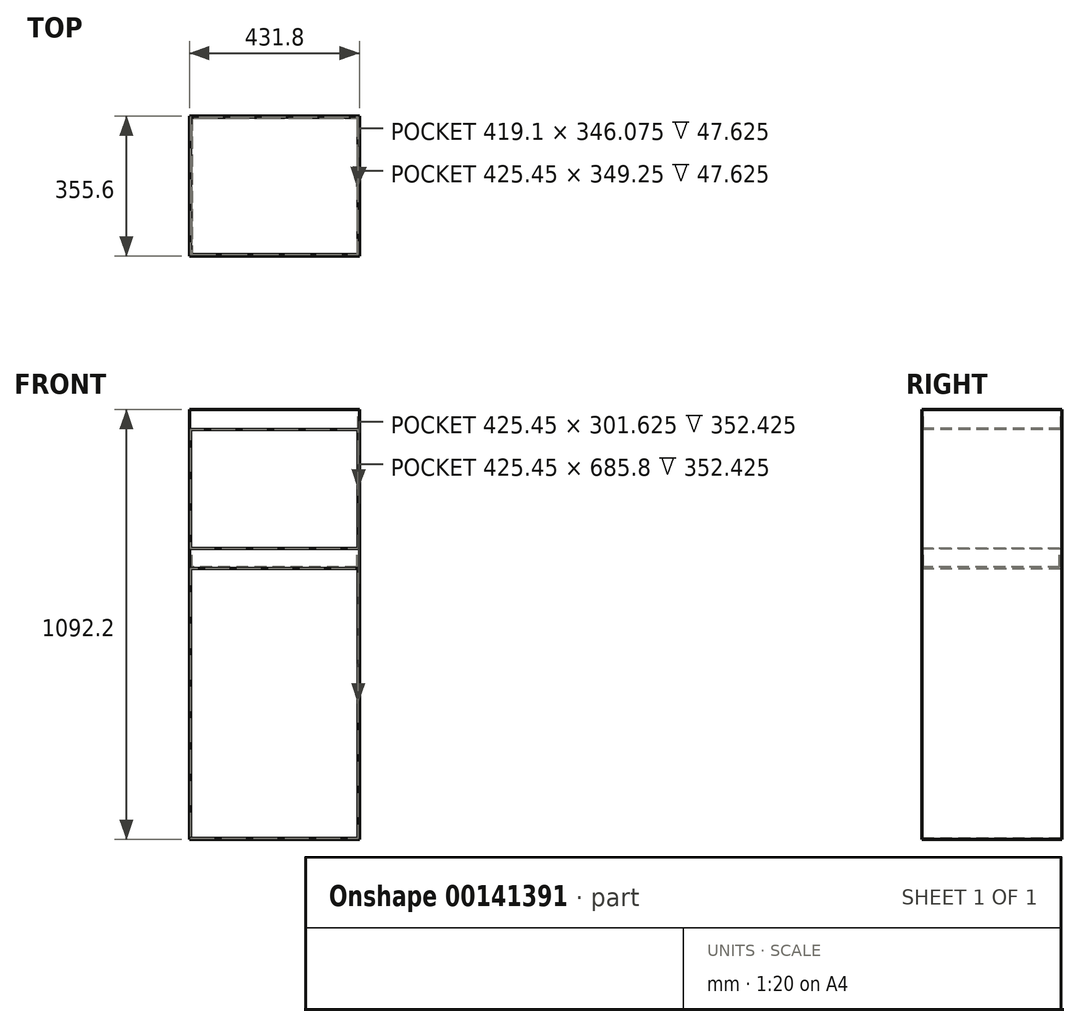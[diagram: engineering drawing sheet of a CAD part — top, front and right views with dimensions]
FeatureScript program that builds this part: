
annotation { "Feature Type Name" : "Feature", "Feature Type Description" : "" }
export const myFeature = defineFeature(function(context is Context, id is Id, definition is map)
    precondition{}
    {
        {
            var Q0;
            Q0=qCreatedBy(makeId("Front.planeOp"),FACE);
            var sketch = newSketch(context, id + "F0", { "sketchPlane" : qUnion([Q0])});
            skLineSegment(sketch, "E0.bottom", {"start": v(-215.9, 546.1) * mm, "end": v(215.9, 546.1) * mm});
            skLineSegment(sketch, "E0.top", {"start": v(-215.9, -546.1) * mm, "end": v(215.9, -546.1) * mm});
            skLineSegment(sketch, "E0.left", {"start": v(-215.9, 546.1) * mm, "end": v(-215.9, -546.1) * mm});
            skLineSegment(sketch, "E0.right", {"start": v(215.9, 546.1) * mm, "end": v(215.9, -546.1) * mm});
            skPoint(sketch, "E0.middle", {"position": v(0, 0) * mm});
            skSolve(sketch);
        }
        {
            var Q0;
            Q0 = qSketchRegion(id + "F0", true);
            extrude(context, id + "F1", {"entities" : qUnion([Q0]), "depth" : 355.6 * mm});
        }
        {
            var Q0;
            Q0=makeQuery(id+"F1.opExtrude","CAP_FACE",FACE,{"disambiguationData":[OSD([sQuery(id+"F0.wireOp",EDGE,"E0.bottom"),sQuery(id+"F0.wireOp",EDGE,"E0.top"),sQuery(id+"F0.wireOp",EDGE,"E0.left"),sQuery(id+"F0.wireOp",EDGE,"E0.right")])],"isStart":false});
            var sketch = newSketch(context, id + "F2", { "sketchPlane" : qUnion([Q0])});
            skLineSegment(sketch, "E1.bottom", {"start": v(-212.72, 495.3) * mm, "end": v(212.73, 495.3) * mm});
            skLineSegment(sketch, "E1.top", {"start": v(-212.72, -542.92) * mm, "end": v(212.73, -542.92) * mm});
            skLineSegment(sketch, "E1.left", {"start": v(-212.72, 495.3) * mm, "end": v(-212.73, -542.92) * mm});
            skLineSegment(sketch, "E1.right", {"start": v(212.72, 495.3) * mm, "end": v(212.73, -542.92) * mm});
            skSolve(sketch);
        }
        {
            var Q0;
            Q0 = qSketchRegion(id + "F2", true);
            extrude(context, id + "F3", {"entities" : qUnion([Q0]), "operationType" : NewBodyOperationType.REMOVE, "oppositeDirection" : true, "depth" : 352.42 * mm});
        }
        {
            var Q0;
            Q0=makeQuery(id+"F3.boolean.opBoolean","COPY",FACE,{"derivedFrom":makeQuery(id+"F3.opExtrude","CAP_FACE",FACE,{"disambiguationData":[OSD([sQuery(id+"F2.wireOp",EDGE,"E1.bottom"),sQuery(id+"F2.wireOp",EDGE,"E1.top"),sQuery(id+"F2.wireOp",EDGE,"E1.left"),sQuery(id+"F2.wireOp",EDGE,"E1.right")])],"isStart":false})});
            var sketch = newSketch(context, id + "F4", { "sketchPlane" : qUnion([Q0])});
            skLineSegment(sketch, "E2.bottom", {"start": v(-212.72, 193.68) * mm, "end": v(212.73, 193.68) * mm});
            skLineSegment(sketch, "E2.top", {"start": v(-212.72, 142.88) * mm, "end": v(212.73, 142.88) * mm});
            skLineSegment(sketch, "E2.left", {"start": v(-212.72, 193.68) * mm, "end": v(-212.72, 142.88) * mm});
            skLineSegment(sketch, "E2.right", {"start": v(212.73, 193.68) * mm, "end": v(212.73, 142.88) * mm});
            skSolve(sketch);
        }
        {
            var Q0;
            Q0 = qSketchRegion(id + "F4", true);
            var Q1;
            Q1=makeQuery(id+"F1.opExtrude","CAP_FACE",FACE,{"disambiguationData":[OSD([sQuery(id+"F0.wireOp",EDGE,"E0.bottom"),sQuery(id+"F0.wireOp",EDGE,"E0.top"),sQuery(id+"F0.wireOp",EDGE,"E0.left"),sQuery(id+"F0.wireOp",EDGE,"E0.right")])],"isStart":false});
            extrude(context, id + "F5", {"entities" : qUnion([Q0]), "operationType" : NewBodyOperationType.ADD, "endBound" : BoundingType.UP_TO_SURFACE, "endBoundEntityFace" : qUnion([Q1]), "depth" : 25.4 * mm});
        }
        {
            var Q0;
            Q0=makeQuery(id+"F5.opExtrude","SWEPT_FACE",FACE,{"disambiguationData":[OSD([sQuery(id+"F4.wireOp",EDGE,"E2.bottom")])]});
            var sketch = newSketch(context, id + "F6", { "sketchPlane" : qUnion([Q0])});
            skLineSegment(sketch, "E3.bottom", {"start": v(209.55, -6.35) * mm, "end": v(-209.55, -6.35) * mm});
            skLineSegment(sketch, "E3.top", {"start": v(209.55, -352.42) * mm, "end": v(-209.55, -352.42) * mm});
            skLineSegment(sketch, "E3.left", {"start": v(209.55, -6.35) * mm, "end": v(209.55, -352.42) * mm});
            skLineSegment(sketch, "E3.right", {"start": v(-209.55, -6.35) * mm, "end": v(-209.55, -352.42) * mm});
            skSolve(sketch);
        }
        {
            var Q0;
            Q0 = qSketchRegion(id + "F6", true);
            extrude(context, id + "F7", {"entities" : qUnion([Q0]), "operationType" : NewBodyOperationType.REMOVE, "oppositeDirection" : true, "depth" : 47.62 * mm});
        }
        {
            var Q0;
            Q0=makeQuery(id+"F1.opExtrude","SWEPT_FACE",FACE,{"disambiguationData":[OSD([sQuery(id+"F0.wireOp",EDGE,"E0.bottom")])]});
            var sketch = newSketch(context, id + "F8", { "sketchPlane" : qUnion([Q0])});
            skLineSegment(sketch, "E4.bottom", {"start": v(-212.72, -3.18) * mm, "end": v(212.73, -3.17) * mm});
            skLineSegment(sketch, "E4.top", {"start": v(-212.72, -352.43) * mm, "end": v(212.73, -352.43) * mm});
            skLineSegment(sketch, "E4.left", {"start": v(-212.72, -3.18) * mm, "end": v(-212.72, -352.43) * mm});
            skLineSegment(sketch, "E4.right", {"start": v(212.73, -3.17) * mm, "end": v(212.73, -352.43) * mm});
            skSolve(sketch);
        }
        {
            var Q0;
            Q0 = qSketchRegion(id + "F8", true);
            extrude(context, id + "F9", {"entities" : qUnion([Q0]), "operationType" : NewBodyOperationType.REMOVE, "oppositeDirection" : true, "depth" : 47.62 * mm});
        }
    });
